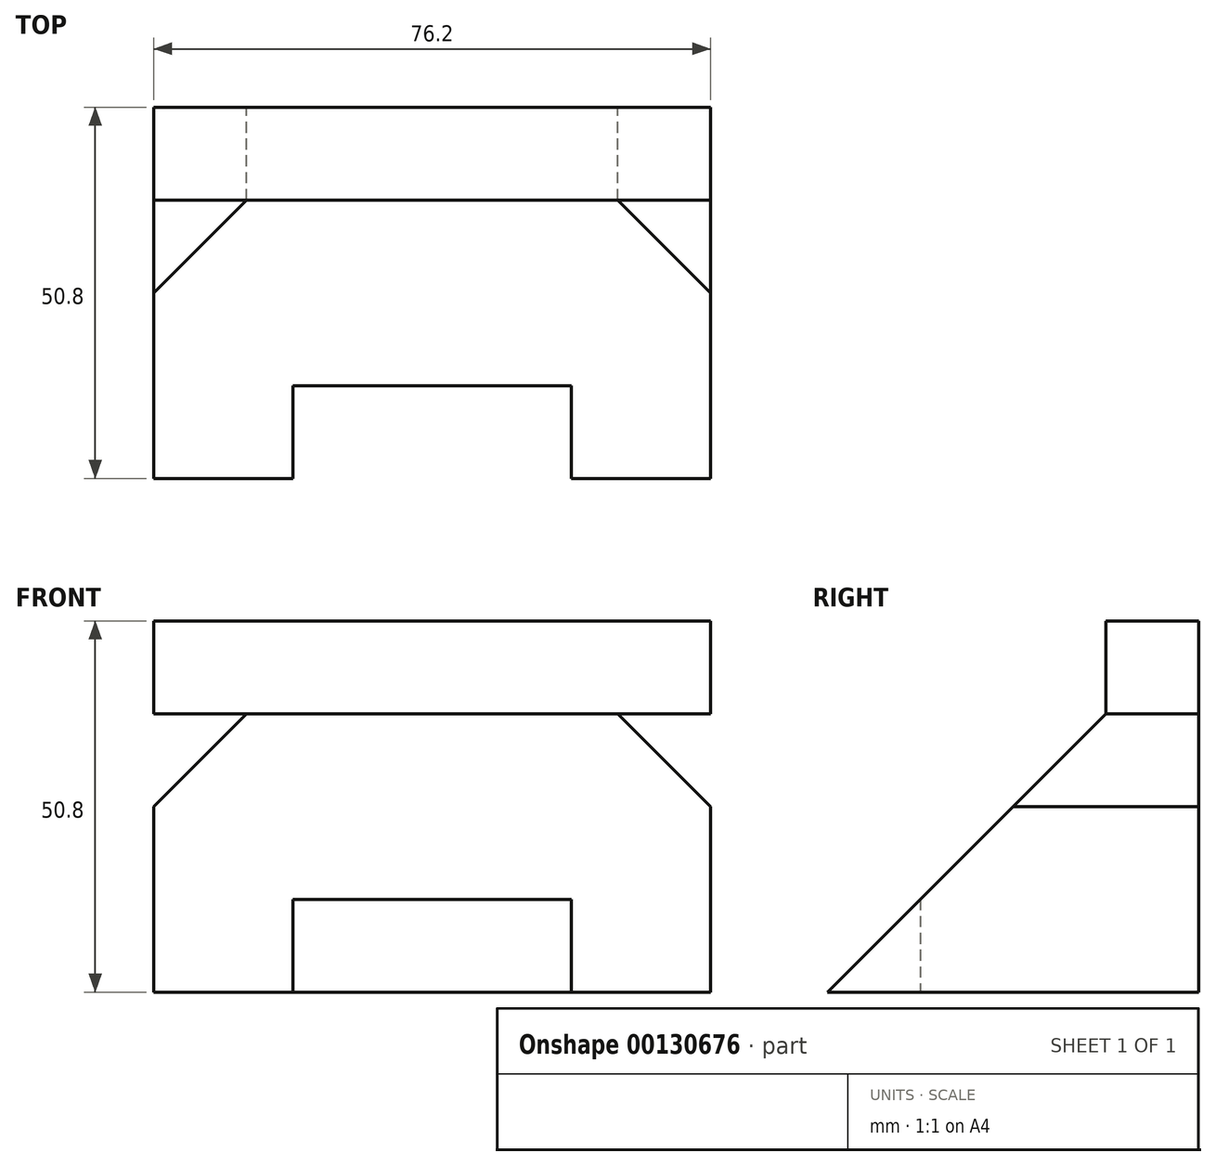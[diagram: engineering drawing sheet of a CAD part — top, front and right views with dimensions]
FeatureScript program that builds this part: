
annotation { "Feature Type Name" : "Feature", "Feature Type Description" : "" }
export const myFeature = defineFeature(function(context is Context, id is Id, definition is map)
    precondition{}
    {
        {
            var Q0;
            Q0=qCreatedBy(makeId("Right.planeOp"),FACE);
            var sketch = newSketch(context, id + "F0", { "sketchPlane" : qUnion([Q0])});
            skLineSegment(sketch, "E0", {"start": v(0, 0) * mm, "end": v(38.1, 0) * mm});
            skLineSegment(sketch, "E1", {"start": v(38.1, 0) * mm, "end": v(38.1, 38.1) * mm});
            skLineSegment(sketch, "E2", {"start": v(38.1, 38.1) * mm, "end": v(0, 0) * mm});
            skLineSegment(sketch, "E3.bottom", {"start": v(38.1, 0) * mm, "end": v(50.8, 0) * mm});
            skLineSegment(sketch, "E3.top", {"start": v(38.1, 50.8) * mm, "end": v(50.8, 50.8) * mm});
            skLineSegment(sketch, "E3.left", {"start": v(38.1, 0) * mm, "end": v(38.1, 50.8) * mm});
            skLineSegment(sketch, "E3.right", {"start": v(50.8, 0) * mm, "end": v(50.8, 50.8) * mm});
            skLineSegment(sketch, "E4", {"start": v(38.1, 25.4) * mm, "end": v(38.1, 0) * mm});
            skLineSegment(sketch, "E5", {"start": v(38.1, 25.4) * mm, "end": v(50.8, 25.4) * mm});
            skLineSegment(sketch, "E6", {"start": v(50.8, 25.4) * mm, "end": v(50.8, 0) * mm});
            skSolve(sketch);
        }
        {
            var Q0;
            Q0 = qSketchRegion(id + "F0", true);
            extrude(context, id + "F1", {"entities" : qUnion([Q0]), "depth" : 76.2 * mm});
        }
        {
            var Q0;
            Q0=makeQuery(id+"F1.opExtrude","SWEPT_FACE",FACE,{"disambiguationData":[OSD([sQuery(id+"F0.wireOp",EDGE,"E0"),sQuery(id+"F0.wireOp",EDGE,"E3.bottom")])]});
            var sketch = newSketch(context, id + "F2", { "sketchPlane" : qUnion([Q0])});
            skLineSegment(sketch, "E7", {"start": v(19.05, 0) * mm, "end": v(57.15, 0) * mm});
            skLineSegment(sketch, "E8", {"start": v(57.15, 0) * mm, "end": v(57.15, -12.7) * mm});
            skLineSegment(sketch, "E9", {"start": v(57.15, -12.7) * mm, "end": v(19.05, -12.7) * mm});
            skLineSegment(sketch, "E10", {"start": v(19.05, -12.7) * mm, "end": v(19.05, 0) * mm});
            skLineSegment(sketch, "E11.0", {"start": v(0, 0) * mm, "end": v(0, -50.8) * mm});
            skLineSegment(sketch, "E12.0", {"start": v(76.2, -50.8) * mm, "end": v(0, -50.8) * mm});
            skLineSegment(sketch, "E13.0", {"start": v(76.2, 0) * mm, "end": v(76.2, -50.8) * mm});
            skLineSegment(sketch, "E14", {"start": v(0, 0) * mm, "end": v(19.05, 0) * mm});
            skLineSegment(sketch, "E15", {"start": v(57.15, 0) * mm, "end": v(76.2, 0) * mm});
            skSolve(sketch);
        }
        {
            var Q0;
            Q0=makeQuery(id+"F2.imprint","IMPRINT",FACE,{"disambiguationData":[TD([[makeQuery(id+"F2.imprint","IMPRINT",EDGE,{"derivedFrom":sQuery(id+"F2.wireOp",EDGE,"E8")}),-1.0]])]});
            extrude(context, id + "F3", {"entities" : qUnion([Q0]), "operationType" : NewBodyOperationType.REMOVE, "endBound" : BoundingType.THROUGH_ALL, "oppositeDirection" : true, "depth" : 25.4 * mm});
        }
        {
            var Q0;
            Q0=makeQuery(id+"F1.opExtrude","SWEPT_FACE",FACE,{"disambiguationData":[OSD([sQuery(id+"F0.wireOp",EDGE,"E3.right"),sQuery(id+"F0.wireOp",EDGE,"E6")])]});
            var sketch = newSketch(context, id + "F4", { "sketchPlane" : qUnion([Q0])});
            skLineSegment(sketch, "E16.top", {"start": v(-76.2, 38.1) * mm, "end": v(0, 38.1) * mm});
            skLineSegment(sketch, "E16.left", {"start": v(-76.2, 50.8) * mm, "end": v(-76.2, 38.1) * mm});
            skLineSegment(sketch, "E16.right", {"start": v(0, 50.8) * mm, "end": v(0, 38.1) * mm});
            skLineSegment(sketch, "E17", {"start": v(-76.2, 50.8) * mm, "end": v(0, 50.8) * mm});
            skLineSegment(sketch, "E18", {"start": v(0, 38.1) * mm, "end": v(0, 0) * mm});
            skLineSegment(sketch, "E19", {"start": v(0, 0) * mm, "end": v(-76.2, 0) * mm});
            skLineSegment(sketch, "E20", {"start": v(-76.2, 0) * mm, "end": v(-76.2, 38.1) * mm});
            skLineSegment(sketch, "E21", {"start": v(-50.8, 50.8) * mm, "end": v(-50.8, 38.1) * mm});
            skLineSegment(sketch, "E22", {"start": v(-25.4, 50.8) * mm, "end": v(-25.4, 38.1) * mm});
            skLineSegment(sketch, "E23", {"start": v(-50.8, 50.8) * mm, "end": v(-76.2, 25.4) * mm});
            skLineSegment(sketch, "E24", {"start": v(-25.4, 50.8) * mm, "end": v(0, 25.4) * mm});
            skSolve(sketch);
        }
        {
            var Q0;
            {var subQ0=sQuery(id+"F4.wireOp",EDGE,"E16.left");Q0=makeQuery(id+"F4.imprint","IMPRINT",FACE,{"disambiguationData":[TD([[makeQuery(id+"F4.imprint","IMPRINT",EDGE,{"derivedFrom":subQ0}),1.0]])]});}
            var Q1;
            {var subQ0=sQuery(id+"F4.wireOp",EDGE,"E16.right");Q1=makeQuery(id+"F4.imprint","IMPRINT",FACE,{"disambiguationData":[TD([[makeQuery(id+"F4.imprint","IMPRINT",EDGE,{"derivedFrom":subQ0}),-1.0]])]});}
            var Q2;
            {var subQ0=sQuery(id+"F4.wireOp",EDGE,"E18");var subQ3=sQuery(id+"F4.wireOp",EDGE,"E24");var subQ5=makeQuery(id+"F4.imprint","INTERSECT",VERTEX,{"derivedFrom":[subQ0,subQ3]});Q2=makeQuery(id+"F4.imprint","IMPRINT",FACE,{"disambiguationData":[TD([[makeQuery(id+"F4.imprint","IMPRINT",EDGE,{"disambiguationData":[TD([[subQ5,1.0]])],"derivedFrom":subQ3}),1.0]])]});}
            var Q3;
            {var subQ0=sQuery(id+"F4.wireOp",EDGE,"E20");var subQ3=sQuery(id+"F4.wireOp",EDGE,"E23");var subQ5=makeQuery(id+"F4.imprint","INTERSECT",VERTEX,{"derivedFrom":[subQ0,subQ3]});Q3=makeQuery(id+"F4.imprint","IMPRINT",FACE,{"disambiguationData":[TD([[makeQuery(id+"F4.imprint","IMPRINT",EDGE,{"disambiguationData":[TD([[subQ5,1.0]])],"derivedFrom":subQ3}),-1.0]])]});}
            extrude(context, id + "F5", {"entities" : qUnion([Q0, Q1, Q2, Q3]), "operationType" : NewBodyOperationType.REMOVE, "endBound" : BoundingType.THROUGH_ALL, "oppositeDirection" : true, "depth" : 25.4 * mm});
        }
    });
